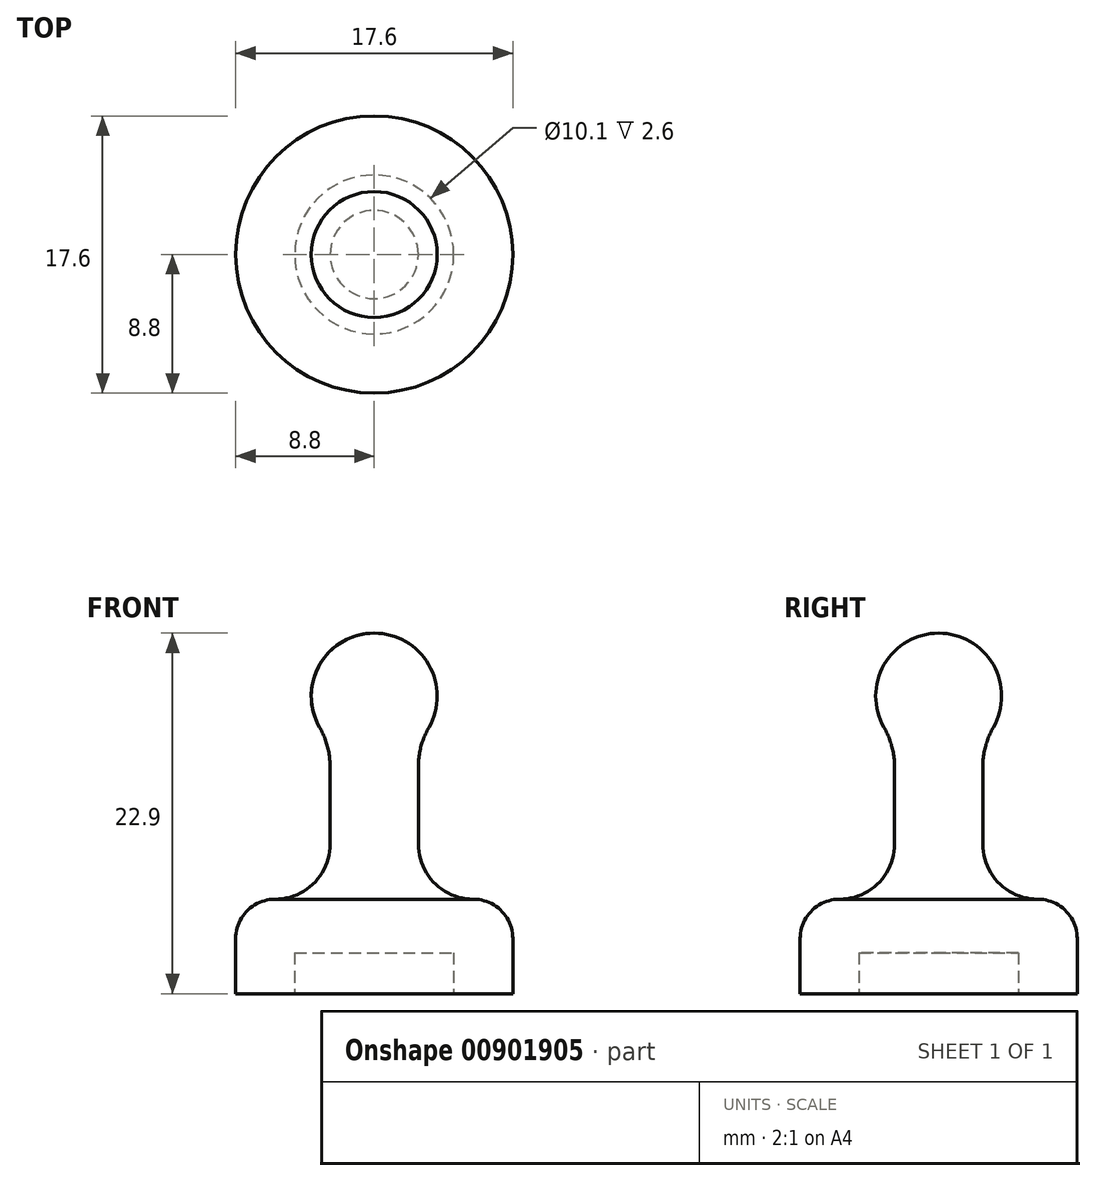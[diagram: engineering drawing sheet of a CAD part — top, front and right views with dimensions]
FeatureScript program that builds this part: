
annotation { "Feature Type Name" : "Feature", "Feature Type Description" : "" }
export const myFeature = defineFeature(function(context is Context, id is Id, definition is map)
    precondition{}
    {
        {
            var Q0;
            Q0=qCreatedBy(makeId("Front.planeOp"),FACE);
            var sketch = newSketch(context, id + "F0", { "sketchPlane" : qUnion([Q0])});
            skLineSegment(sketch, "E0", {"start": v(-3.4, 4.1) * mm, "end": v(-3.4, 24.4) * mm});
            skLineSegment(sketch, "E1", {"start": v(-8.45, 1.5) * mm, "end": v(-12.2, 1.5) * mm});
            skLineSegment(sketch, "E2", {"start": v(-12.2, 1.5) * mm, "end": v(-12.2, 5) * mm});
            skArc(sketch, "E3", {"start": v(-3.4, 24.4) * mm, "mid": v(-6.86, 22.4) * mm, "end": v(-6.87, 18.4) * mm});
            skLineSegment(sketch, "E4", {"start": v(-6.2, 15.91) * mm, "end": v(-6.2, 11) * mm});
            skLineSegment(sketch, "E5", {"start": v(-9.7, 7.5) * mm, "end": v(-9.7, 7.5) * mm});
            skPoint(sketch, "E6.visualSharp", {"position": v(-6.2, 17.54) * mm});
            skArc(sketch, "E6.filletArc", {"start": v(-6.2, 15.91) * mm, "mid": v(-6.37, 17.2) * mm, "end": v(-6.87, 18.4) * mm});
            skPoint(sketch, "E7.visualSharp", {"position": v(-6.2, 7.5) * mm});
            skArc(sketch, "E7.filletArc", {"start": v(-9.7, 7.5) * mm, "mid": v(-7.23, 8.53) * mm, "end": v(-6.2, 11) * mm});
            skPoint(sketch, "E8.visualSharp", {"position": v(-12.2, 7.5) * mm});
            skArc(sketch, "E8.filletArc", {"start": v(-9.7, 7.5) * mm, "mid": v(-11.47, 6.77) * mm, "end": v(-12.2, 5) * mm});
            skLineSegment(sketch, "E9", {"start": v(-3.4, 4.1) * mm, "end": v(-8.45, 4.1) * mm});
            skLineSegment(sketch, "E10", {"start": v(-8.45, 4.1) * mm, "end": v(-8.45, 1.5) * mm});
            skSolve(sketch);
        }
        {
            var Q0;
            Q0=makeQuery(id+"F0.imprint","IMPRINT",FACE,{"disambiguationData":[TD([[makeQuery(id+"F0.imprint","IMPRINT",EDGE,{"derivedFrom":sQuery(id+"F0.wireOp",EDGE,"E0")}),1.0]])]});
            var Q1;
            Q1=sQuery(id+"F0.wireOp",EDGE,"E0");
            revolve(context, id + "F1", {"surfaceOperationType" : NewSurfaceOperationType.NEW, "entities" : qUnion([Q0]), "axis" : qUnion([Q1]), "revolveType" : RevolveType.FULL});
        }
    });
